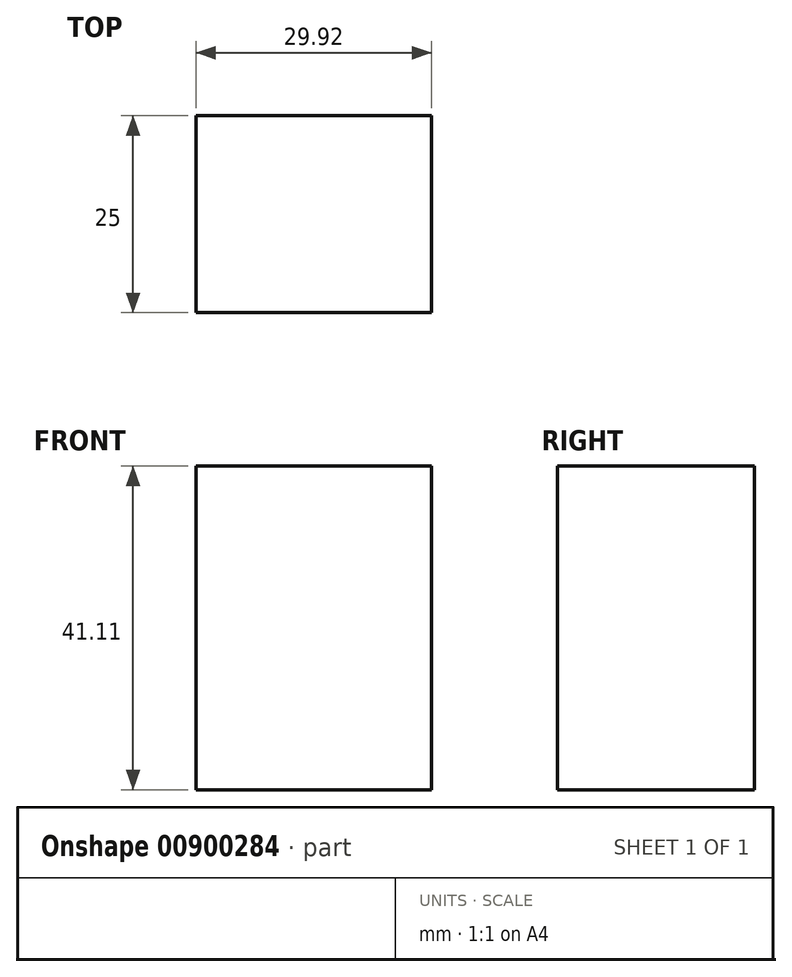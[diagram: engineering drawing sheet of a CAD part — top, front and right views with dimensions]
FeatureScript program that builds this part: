
annotation { "Feature Type Name" : "Feature", "Feature Type Description" : "" }
export const myFeature = defineFeature(function(context is Context, id is Id, definition is map)
    precondition{}
    {
        {
            var Q0;
            Q0=qCreatedBy(makeId("Front.planeOp"),FACE);
            var sketch = newSketch(context, id + "F0", { "sketchPlane" : qUnion([Q0])});
            skLineSegment(sketch, "E0.bottom", {"start": v(-137.66, 50.52) * mm, "end": v(-107.74, 50.52) * mm});
            skLineSegment(sketch, "E0.top", {"start": v(-137.66, 9.4) * mm, "end": v(-107.74, 9.4) * mm});
            skLineSegment(sketch, "E0.left", {"start": v(-137.66, 50.52) * mm, "end": v(-137.66, 9.4) * mm});
            skLineSegment(sketch, "E0.right", {"start": v(-107.74, 50.52) * mm, "end": v(-107.74, 9.4) * mm});
            skSolve(sketch);
        }
        {
            var Q0;
            Q0 = qSketchRegion(id + "F0", true);
            extrude(context, id + "F1", {"entities" : qUnion([Q0]), "depth" : 25 * mm, "offsetDistance" : 25 * mm});
        }
    });
